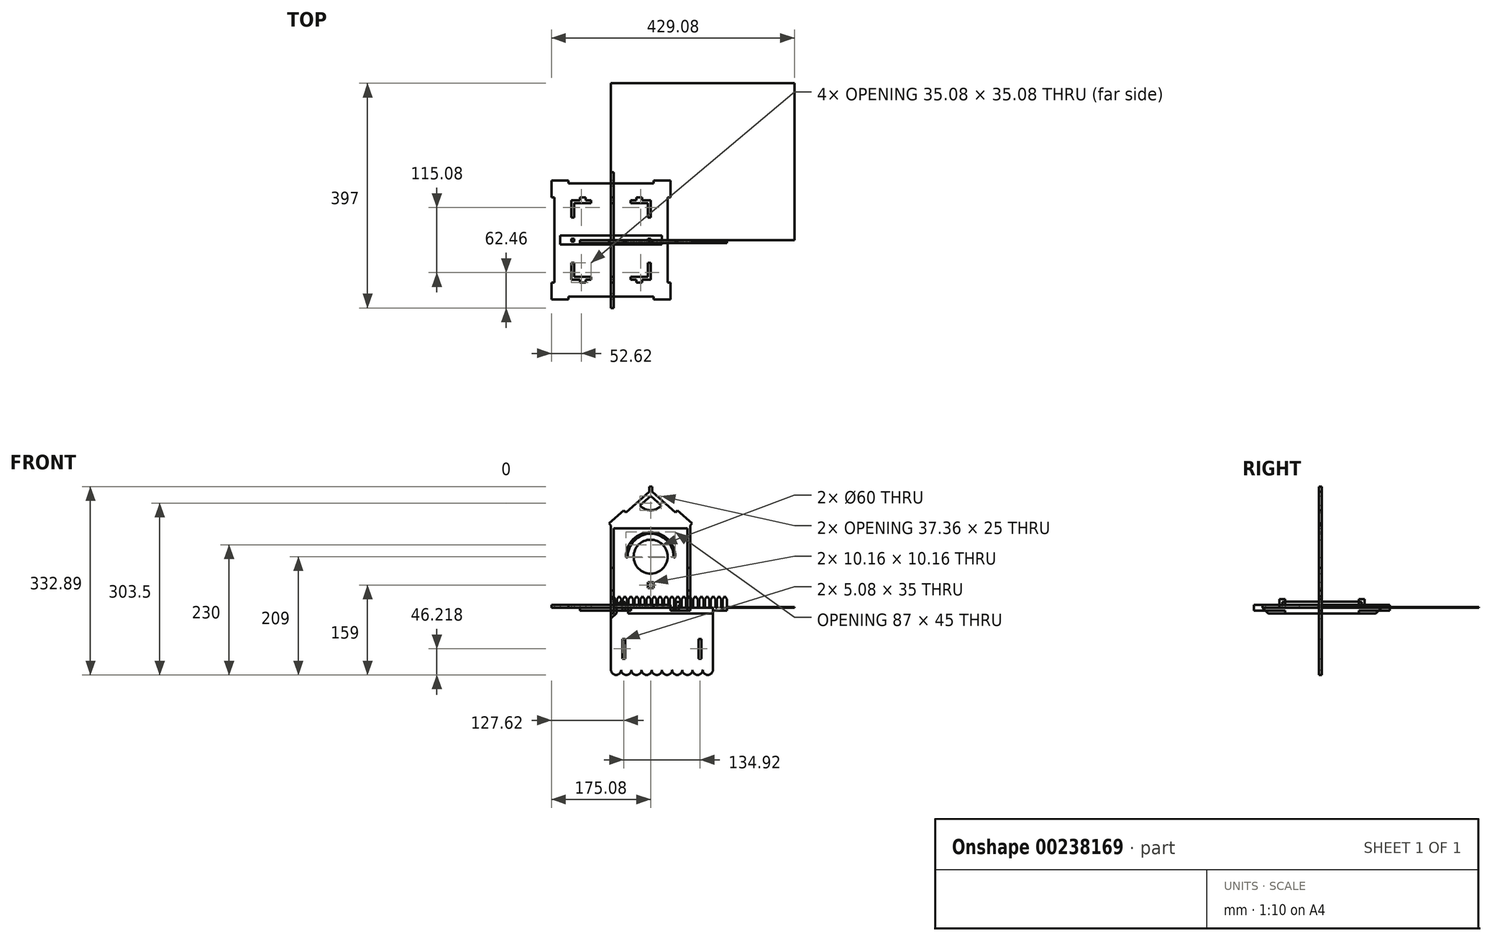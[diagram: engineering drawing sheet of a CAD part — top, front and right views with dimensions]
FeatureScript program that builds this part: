
annotation { "Feature Type Name" : "Feature", "Feature Type Description" : "" }
export const myFeature = defineFeature(function(context is Context, id is Id, definition is map)
    precondition{}
    {
        {
            var Q0;
            Q0=qCreatedBy(makeId("Front.planeOp"),FACE);
            var sketch = newSketch(context, id + "F0", { "sketchPlane" : qUnion([Q0])});
            skLineSegment(sketch, "E0.left", {"start": v(0, 30) * mm, "end": v(0, 70) * mm});
            skLineSegment(sketch, "E1", {"start": v(0, 30) * mm, "end": v(5.08, 30) * mm});
            skLineSegment(sketch, "E2", {"start": v(0, 70) * mm, "end": v(5.08, 70) * mm});
            skLineSegment(sketch, "E3", {"start": v(5.08, 70) * mm, "end": v(5.08, 140) * mm});
            skLineSegment(sketch, "E4", {"start": v(5.08, 30) * mm, "end": v(5.08, -5.08) * mm});
            skLineSegment(sketch, "E5", {"start": v(134.92, 140) * mm, "end": v(134.92, 70) * mm});
            skLineSegment(sketch, "E6", {"start": v(134.92, 70) * mm, "end": v(140, 70) * mm});
            skLineSegment(sketch, "E7", {"start": v(140, 70) * mm, "end": v(140, 30) * mm});
            skLineSegment(sketch, "E8", {"start": v(140, 30) * mm, "end": v(134.92, 30) * mm});
            skLineSegment(sketch, "E9", {"start": v(134.92, 30) * mm, "end": v(134.92, -5.08) * mm});
            skLineSegment(sketch, "E10", {"start": v(70, 145.26) * mm, "end": v(70, -12.71) * mm, "construction": true});
            skCircle(sketch, "E11", {"center": v(70, 90) * mm, "radius": 30 * mm});
            skLineSegment(sketch, "E12.bottom", {"start": v(75.08, 45.08) * mm, "end": v(64.92, 45.08) * mm});
            skLineSegment(sketch, "E12.top", {"start": v(75.08, 34.92) * mm, "end": v(64.92, 34.92) * mm});
            skLineSegment(sketch, "E12.left", {"start": v(75.08, 45.08) * mm, "end": v(75.08, 34.92) * mm});
            skLineSegment(sketch, "E12.right", {"start": v(64.92, 45.08) * mm, "end": v(64.92, 34.92) * mm});
            skPoint(sketch, "E12.middle", {"position": v(70, 40) * mm});
            skLineSegment(sketch, "E13", {"start": v(5.08, -5.08) * mm, "end": v(20.32, -5.08) * mm});
            skLineSegment(sketch, "E14", {"start": v(20.32, -5.08) * mm, "end": v(20.32, 5.08) * mm});
            skLineSegment(sketch, "E15", {"start": v(20.32, 5.08) * mm, "end": v(15.24, 5.08) * mm});
            skLineSegment(sketch, "E16", {"start": v(15.24, 5.08) * mm, "end": v(15.24, 10.16) * mm});
            skLineSegment(sketch, "E17", {"start": v(15.24, 10.16) * mm, "end": v(25.4, 10.16) * mm});
            skLineSegment(sketch, "E18", {"start": v(25.4, 10.16) * mm, "end": v(25.4, -5.08) * mm});
            skLineSegment(sketch, "E19", {"start": v(25.4, -5.08) * mm, "end": v(35.08, -5.08) * mm});
            skLineSegment(sketch, "E20", {"start": v(35.08, -5.08) * mm, "end": v(35.08, 0) * mm});
            skLineSegment(sketch, "E21", {"start": v(134.92, -5.08) * mm, "end": v(119.68, -5.08) * mm});
            skLineSegment(sketch, "E22", {"start": v(119.68, -5.08) * mm, "end": v(119.68, 5.08) * mm});
            skLineSegment(sketch, "E23", {"start": v(119.68, 5.08) * mm, "end": v(124.76, 5.08) * mm});
            skLineSegment(sketch, "E24", {"start": v(124.76, 5.08) * mm, "end": v(124.76, 10.16) * mm});
            skLineSegment(sketch, "E25", {"start": v(124.76, 10.16) * mm, "end": v(114.6, 10.16) * mm});
            skLineSegment(sketch, "E26", {"start": v(114.6, 10.16) * mm, "end": v(114.6, -5.08) * mm});
            skLineSegment(sketch, "E27", {"start": v(114.6, -5.08) * mm, "end": v(104.92, -5.08) * mm});
            skLineSegment(sketch, "E28", {"start": v(104.92, -5.08) * mm, "end": v(104.92, 0) * mm});
            skLineSegment(sketch, "E29", {"start": v(5.08, 140) * mm, "end": v(134.92, 140) * mm});
            skLineSegment(sketch, "E30", {"start": v(35.08, 0) * mm, "end": v(104.92, 0) * mm});
            skSolve(sketch);
        }
        {
            var Q0;
            Q0 = qSketchRegion(id + "F0", true);
            extrude(context, id + "F1", {"entities" : qUnion([Q0]), "depth" : 5.08 * mm});
        }
        {
            var Q0;
            Q0=qCreatedBy(makeId("Front.planeOp"),FACE);
            var sketch = newSketch(context, id + "F2", { "sketchPlane" : qUnion([Q0])});
            skLineSegment(sketch, "E31.left", {"start": v(0, 0) * mm, "end": v(0, 30) * mm});
            skLineSegment(sketch, "E32", {"start": v(0, 70) * mm, "end": v(5.08, 70) * mm});
            skLineSegment(sketch, "E33", {"start": v(5.08, 70) * mm, "end": v(5.08, 30) * mm});
            skLineSegment(sketch, "E34", {"start": v(5.08, 30) * mm, "end": v(0, 30) * mm});
            skLineSegment(sketch, "E35.trimOffspring", {"start": v(0, 70) * mm, "end": v(0, 145) * mm});
            skLineSegment(sketch, "E36", {"start": v(70, -4.41) * mm, "end": v(70, 218.12) * mm, "construction": true});
            skLineSegment(sketch, "E37", {"start": v(140, 0) * mm, "end": v(140, 30) * mm});
            skLineSegment(sketch, "E38", {"start": v(140, 30) * mm, "end": v(134.92, 30) * mm});
            skLineSegment(sketch, "E39", {"start": v(134.92, 30) * mm, "end": v(134.92, 70) * mm});
            skLineSegment(sketch, "E40", {"start": v(134.92, 70) * mm, "end": v(140, 70) * mm});
            skLineSegment(sketch, "E41", {"start": v(140, 70) * mm, "end": v(140, 145) * mm});
            skLineSegment(sketch, "E42", {"start": v(26.15, 168.26) * mm, "end": v(67.46, 205) * mm});
            skLineSegment(sketch, "E43", {"start": v(0, 145) * mm, "end": v(-3.38, 148.8) * mm});
            skLineSegment(sketch, "E44", {"start": v(-3.38, 148.8) * mm, "end": v(22.78, 172.06) * mm});
            skLineSegment(sketch, "E45", {"start": v(22.78, 172.06) * mm, "end": v(26.15, 168.26) * mm});
            skLineSegment(sketch, "E46", {"start": v(0, 145) * mm, "end": v(26.15, 168.26) * mm, "construction": true});
            skLineSegment(sketch, "E47", {"start": v(140, 145) * mm, "end": v(143.38, 148.8) * mm});
            skLineSegment(sketch, "E48", {"start": v(143.38, 148.8) * mm, "end": v(117.22, 172.06) * mm});
            skLineSegment(sketch, "E49", {"start": v(117.22, 172.06) * mm, "end": v(113.85, 168.26) * mm});
            skLineSegment(sketch, "E50", {"start": v(67.46, 205) * mm, "end": v(67.46, 213.89) * mm});
            skLineSegment(sketch, "E51", {"start": v(67.46, 213.89) * mm, "end": v(70, 213.89) * mm});
            skLineSegment(sketch, "E52", {"start": v(113.85, 168.26) * mm, "end": v(72.54, 205) * mm});
            skLineSegment(sketch, "E53", {"start": v(72.54, 205) * mm, "end": v(72.54, 213.89) * mm});
            skLineSegment(sketch, "E54", {"start": v(72.54, 213.89) * mm, "end": v(70, 213.89) * mm});
            skLineSegment(sketch, "E55", {"start": v(70, 197) * mm, "end": v(51.32, 180.39) * mm});
            skLineSegment(sketch, "E56", {"start": v(70, 197) * mm, "end": v(88.68, 180.39) * mm});
            skArc(sketch, "E57", {"start": v(88.68, 180.39) * mm, "mid": v(70, 172) * mm, "end": v(51.32, 180.39) * mm});
            skLineSegment(sketch, "E58", {"start": v(0, 0) * mm, "end": v(0, -5.08) * mm});
            skLineSegment(sketch, "E59", {"start": v(0, -5.08) * mm, "end": v(30, -5.08) * mm});
            skLineSegment(sketch, "E60", {"start": v(30, -5.08) * mm, "end": v(30, 0) * mm});
            skLineSegment(sketch, "E61", {"start": v(140, 0) * mm, "end": v(140, -5.08) * mm});
            skLineSegment(sketch, "E62", {"start": v(140, -5.08) * mm, "end": v(110, -5.08) * mm});
            skLineSegment(sketch, "E63", {"start": v(110, -5.08) * mm, "end": v(110, 0) * mm});
            skLineSegment(sketch, "E64", {"start": v(30, 0) * mm, "end": v(110, 0) * mm});
            skSolve(sketch);
        }
        {
            var Q0;
            Q0 = qSketchRegion(id + "F2", true);
            extrude(context, id + "F3", {"entities" : qUnion([Q0]), "depth" : 5.08 * mm});
        }
        {
            var Q0;
            Q0=qCreatedBy(makeId("Front.planeOp"),FACE);
            var sketch = newSketch(context, id + "F4", { "sketchPlane" : qUnion([Q0])});
            skLineSegment(sketch, "E65.left", {"start": v(0, 0) * mm, "end": v(0, 30) * mm});
            skLineSegment(sketch, "E66", {"start": v(0, 70) * mm, "end": v(5.08, 70) * mm});
            skLineSegment(sketch, "E67", {"start": v(5.08, 70) * mm, "end": v(5.08, 30) * mm});
            skLineSegment(sketch, "E68", {"start": v(5.08, 30) * mm, "end": v(0, 30) * mm});
            skLineSegment(sketch, "E69.trimOffspring", {"start": v(0, 70) * mm, "end": v(0, 145) * mm});
            skLineSegment(sketch, "E70", {"start": v(70, -55.12) * mm, "end": v(70, 167.4) * mm, "construction": true});
            skLineSegment(sketch, "E71", {"start": v(140, 0) * mm, "end": v(140, 30) * mm});
            skLineSegment(sketch, "E72", {"start": v(140, 30) * mm, "end": v(134.92, 30) * mm});
            skLineSegment(sketch, "E73", {"start": v(134.92, 30) * mm, "end": v(134.92, 70) * mm});
            skLineSegment(sketch, "E74", {"start": v(134.92, 70) * mm, "end": v(140, 70) * mm});
            skLineSegment(sketch, "E75", {"start": v(140, 70) * mm, "end": v(140, 145) * mm});
            skLineSegment(sketch, "E76", {"start": v(26.15, 168.26) * mm, "end": v(67.46, 205) * mm});
            skLineSegment(sketch, "E77", {"start": v(0, 145) * mm, "end": v(-3.38, 148.8) * mm});
            skLineSegment(sketch, "E78", {"start": v(-3.38, 148.8) * mm, "end": v(22.78, 172.06) * mm});
            skLineSegment(sketch, "E79", {"start": v(22.78, 172.06) * mm, "end": v(26.15, 168.26) * mm});
            skLineSegment(sketch, "E80", {"start": v(0, 145) * mm, "end": v(26.15, 168.26) * mm, "construction": true});
            skLineSegment(sketch, "E81", {"start": v(140, 145) * mm, "end": v(143.38, 148.8) * mm});
            skLineSegment(sketch, "E82", {"start": v(143.38, 148.8) * mm, "end": v(117.22, 172.06) * mm});
            skLineSegment(sketch, "E83", {"start": v(117.22, 172.06) * mm, "end": v(113.85, 168.26) * mm});
            skLineSegment(sketch, "E84", {"start": v(67.46, 205) * mm, "end": v(67.46, 213.9) * mm});
            skLineSegment(sketch, "E85", {"start": v(67.46, 213.89) * mm, "end": v(70, 213.89) * mm});
            skLineSegment(sketch, "E86", {"start": v(113.85, 168.26) * mm, "end": v(72.54, 205) * mm});
            skLineSegment(sketch, "E87", {"start": v(72.54, 205) * mm, "end": v(72.54, 213.9) * mm});
            skLineSegment(sketch, "E88", {"start": v(72.54, 213.9) * mm, "end": v(70, 213.9) * mm});
            skLineSegment(sketch, "E89", {"start": v(70, 197) * mm, "end": v(51.32, 180.39) * mm});
            skLineSegment(sketch, "E90", {"start": v(70, 197) * mm, "end": v(88.68, 180.39) * mm});
            skArc(sketch, "E91", {"start": v(88.68, 180.39) * mm, "mid": v(70, 172) * mm, "end": v(51.32, 180.39) * mm});
            skCircle(sketch, "E92", {"center": v(70, 90) * mm, "radius": 30 * mm});
            skArc(sketch, "E93", {"start": v(28, 90) * mm, "mid": v(70, 132) * mm, "end": v(112, 90) * mm});
            skArc(sketch, "E94.0.startCap", {"start": v(29.5, 90) * mm, "mid": v(28, 88.5) * mm, "end": v(26.5, 90) * mm});
            skArc(sketch, "E94.0.endCap", {"start": v(113.5, 90) * mm, "mid": v(112, 88.5) * mm, "end": v(110.5, 90) * mm});
            skArc(sketch, "E94.0.left", {"start": v(26.5, 90) * mm, "mid": v(70, 133.5) * mm, "end": v(113.5, 90) * mm});
            skArc(sketch, "E94.0.right", {"start": v(29.5, 90) * mm, "mid": v(70, 130.5) * mm, "end": v(110.5, 90) * mm});
            skLineSegment(sketch, "E95.bottom", {"start": v(75.08, 45.08) * mm, "end": v(64.92, 45.08) * mm});
            skLineSegment(sketch, "E95.top", {"start": v(75.08, 34.92) * mm, "end": v(64.92, 34.92) * mm});
            skLineSegment(sketch, "E95.left", {"start": v(75.08, 45.08) * mm, "end": v(75.08, 34.92) * mm});
            skLineSegment(sketch, "E95.right", {"start": v(64.92, 45.08) * mm, "end": v(64.92, 34.92) * mm});
            skPoint(sketch, "E95.middle", {"position": v(70, 40) * mm});
            skLineSegment(sketch, "E96", {"start": v(0, 0) * mm, "end": v(0, -5.08) * mm});
            skLineSegment(sketch, "E97", {"start": v(0, -5.08) * mm, "end": v(30, -5.08) * mm});
            skLineSegment(sketch, "E98", {"start": v(30, -5.08) * mm, "end": v(30, 0) * mm});
            skLineSegment(sketch, "E99", {"start": v(140, 0) * mm, "end": v(140, -5.08) * mm});
            skLineSegment(sketch, "E100", {"start": v(140, -5.08) * mm, "end": v(110, -5.08) * mm});
            skLineSegment(sketch, "E101", {"start": v(110, -5.08) * mm, "end": v(110, 0) * mm});
            skLineSegment(sketch, "E102", {"start": v(30, 0) * mm, "end": v(110, 0) * mm});
            skSolve(sketch);
        }
        {
            var Q0;
            Q0 = qSketchRegion(id + "F4", true);
            extrude(context, id + "F5", {"entities" : qUnion([Q0]), "depth" : 5.08 * mm});
        }
        {
            var Q0;
            Q0=qCreatedBy(makeId("Right.planeOp"),FACE);
            var sketch = newSketch(context, id + "F6", { "sketchPlane" : qUnion([Q0])});
            skLineSegment(sketch, "E103.bottom", {"start": v(64.92, 10.26) * mm, "end": v(-64.92, 10.26) * mm});
            skLineSegment(sketch, "E103.top", {"start": v(64.92, -10.26) * mm, "end": v(-64.92, -10.26) * mm});
            skLineSegment(sketch, "E103.left", {"start": v(64.92, 10.26) * mm, "end": v(64.92, 5.08) * mm});
            skLineSegment(sketch, "E103.right", {"start": v(-64.92, 10.26) * mm, "end": v(-64.92, 5.08) * mm});
            skPoint(sketch, "E103.middle", {"position": v(0, 0) * mm});
            skLineSegment(sketch, "E104.bottom", {"start": v(120, 5.08) * mm, "end": v(64.92, 5.08) * mm});
            skLineSegment(sketch, "E104.top", {"start": v(120, -5.08) * mm, "end": v(64.92, -5.08) * mm});
            skLineSegment(sketch, "E104.left", {"start": v(120, 5.08) * mm, "end": v(120, -5.08) * mm});
            skLineSegment(sketch, "E104.right", {"start": v(-120, 5.08) * mm, "end": v(-120, -5.08) * mm});
            skLineSegment(sketch, "E105.trimOffspring", {"start": v(-64.92, 5.08) * mm, "end": v(-120, 5.08) * mm});
            skLineSegment(sketch, "E106.trimOffspring", {"start": v(-64.92, -5.08) * mm, "end": v(-120, -5.08) * mm});
            skLineSegment(sketch, "E107.trimOffspring", {"start": v(-64.92, -5.08) * mm, "end": v(-64.92, -10.26) * mm});
            skLineSegment(sketch, "E108.trimOffspring", {"start": v(64.92, -5.08) * mm, "end": v(64.92, -10.26) * mm});
            skSolve(sketch);
        }
        {
            var Q0;
            Q0 = qSketchRegion(id + "F6", true);
            extrude(context, id + "F7", {"entities" : qUnion([Q0]), "depth" : 5.08 * mm});
        }
        {
            var Q0;
            Q0=qCreatedBy(makeId("Front.planeOp"),FACE);
            var sketch = newSketch(context, id + "F8", { "sketchPlane" : qUnion([Q0])});
            skLineSegment(sketch, "E109", {"start": v(-91.76, 0) * mm, "end": v(91.72, 0) * mm, "construction": true});
            skLineSegment(sketch, "E110", {"start": v(-55.08, 5.08) * mm, "end": v(0, 5.08) * mm});
            skLineSegment(sketch, "E111", {"start": v(0, 5.08) * mm, "end": v(0, 19.08) * mm});
            skLineSegment(sketch, "E112", {"start": v(0, 19.08) * mm, "end": v(10.16, 9.54) * mm});
            skLineSegment(sketch, "E113.MirrorCS", {"start": v(0, -19.08) * mm, "end": v(10.16, -9.54) * mm});
            skLineSegment(sketch, "E114.MirrorCS", {"start": v(-55.08, -5.08) * mm, "end": v(0, -5.08) * mm});
            skLineSegment(sketch, "E115.MirrorCS", {"start": v(0, -5.08) * mm, "end": v(0, -19.08) * mm});
            skLineSegment(sketch, "E116", {"start": v(-55.08, 5.08) * mm, "end": v(-55.08, -5.08) * mm});
            skLineSegment(sketch, "E117", {"start": v(10.16, 9.54) * mm, "end": v(10.16, -9.54) * mm});
            skSolve(sketch);
        }
        {
            var Q0;
            Q0 = qSketchRegion(id + "F8", true);
            extrude(context, id + "F9", {"entities" : qUnion([Q0]), "depth" : 5.08 * mm});
        }
        {
            var Q0;
            Q0=qCreatedBy(makeId("Top.planeOp"),FACE);
            var sketch = newSketch(context, id + "F10", { "sketchPlane" : qUnion([Q0])});
            skLineSegment(sketch, "E118.bottom", {"start": v(100, 100) * mm, "end": v(-100, 100) * mm, "construction": true});
            skLineSegment(sketch, "E118.top", {"start": v(100, -100) * mm, "end": v(-100, -100) * mm, "construction": true});
            skLineSegment(sketch, "E118.left", {"start": v(100, 100) * mm, "end": v(100, -100) * mm, "construction": true});
            skLineSegment(sketch, "E118.right", {"start": v(-100, 100) * mm, "end": v(-100, -100) * mm, "construction": true});
            skPoint(sketch, "E118.middle", {"position": v(0, 0) * mm});
            skLineSegment(sketch, "E119.bottom", {"start": v(70, -70) * mm, "end": v(-70, -70) * mm, "construction": true});
            skLineSegment(sketch, "E119.top", {"start": v(70, 70) * mm, "end": v(-70, 70) * mm, "construction": true});
            skLineSegment(sketch, "E119.left", {"start": v(70, -70) * mm, "end": v(70, 70) * mm, "construction": true});
            skLineSegment(sketch, "E119.right", {"start": v(-70, -70) * mm, "end": v(-70, 70) * mm, "construction": true});
            skLineSegment(sketch, "E120", {"start": v(-70, 70) * mm, "end": v(-54.76, 70) * mm});
            skLineSegment(sketch, "E121", {"start": v(-34.92, 64.92) * mm, "end": v(-64.92, 64.92) * mm});
            skLineSegment(sketch, "E122", {"start": v(-64.92, 64.92) * mm, "end": v(-64.92, 40) * mm});
            skLineSegment(sketch, "E123", {"start": v(-64.92, 40) * mm, "end": v(-70, 40) * mm});
            skLineSegment(sketch, "E124", {"start": v(-70, 40) * mm, "end": v(-70, 70) * mm});
            skLineSegment(sketch, "E125", {"start": v(0, 100.63) * mm, "end": v(0, -98.34) * mm, "construction": true});
            skLineSegment(sketch, "E126", {"start": v(-101.52, 0) * mm, "end": v(102.53, 0) * mm, "construction": true});
            skPoint(sketch, "E126.endSnap0", {"position": v(70, 0) * mm});
            skPoint(sketch, "E127.MirrorP", {"position": v(-70, 0) * mm});
            skLineSegment(sketch, "E128", {"start": v(-100, 75.08) * mm, "end": v(-105.08, 75.08) * mm});
            skLineSegment(sketch, "E129", {"start": v(-105.08, 75.08) * mm, "end": v(-105.08, 105.08) * mm});
            skLineSegment(sketch, "E130", {"start": v(-105.08, 105.08) * mm, "end": v(-75.08, 105.08) * mm});
            skLineSegment(sketch, "E131", {"start": v(-75.08, 105.08) * mm, "end": v(-75.08, 100) * mm});
            skLineSegment(sketch, "E132.MirrorCS", {"start": v(75.08, 105.08) * mm, "end": v(75.08, 100) * mm});
            skLineSegment(sketch, "E133.MirrorCS", {"start": v(105.08, 105.08) * mm, "end": v(75.08, 105.08) * mm});
            skLineSegment(sketch, "E134.MirrorCS", {"start": v(100, 75.08) * mm, "end": v(105.08, 75.08) * mm});
            skLineSegment(sketch, "E135.MirrorCS", {"start": v(105.08, 75.08) * mm, "end": v(105.08, 105.08) * mm});
            skLineSegment(sketch, "E136", {"start": v(-75.08, 100) * mm, "end": v(75.08, 100) * mm});
            skLineSegment(sketch, "E137.MirrorCS", {"start": v(100, -75.08) * mm, "end": v(105.08, -75.08) * mm});
            skLineSegment(sketch, "E138.MirrorCS", {"start": v(105.08, -75.08) * mm, "end": v(105.08, -105.08) * mm});
            skLineSegment(sketch, "E139.MirrorCS", {"start": v(105.08, -105.08) * mm, "end": v(75.08, -105.08) * mm});
            skLineSegment(sketch, "E140.MirrorCS", {"start": v(75.08, -105.08) * mm, "end": v(75.08, -100) * mm});
            skLineSegment(sketch, "E141.MirrorCS", {"start": v(-75.08, -100) * mm, "end": v(75.08, -100) * mm});
            skLineSegment(sketch, "E142.MirrorCS", {"start": v(-75.08, -105.08) * mm, "end": v(-75.08, -100) * mm});
            skLineSegment(sketch, "E143.MirrorCS", {"start": v(-105.08, -105.08) * mm, "end": v(-75.08, -105.08) * mm});
            skLineSegment(sketch, "E144.MirrorCS", {"start": v(-100, -75.08) * mm, "end": v(-105.08, -75.08) * mm});
            skLineSegment(sketch, "E145.MirrorCS", {"start": v(-105.08, -75.08) * mm, "end": v(-105.08, -105.08) * mm});
            skLineSegment(sketch, "E146", {"start": v(-100, 75.08) * mm, "end": v(-100, -75.08) * mm});
            skLineSegment(sketch, "E147", {"start": v(100, 75.08) * mm, "end": v(100, -75.08) * mm});
            skLineSegment(sketch, "E148", {"start": v(-54.76, 70) * mm, "end": v(-54.76, 75.08) * mm});
            skLineSegment(sketch, "E149", {"start": v(-54.76, 75.08) * mm, "end": v(-44.6, 75.08) * mm});
            skLineSegment(sketch, "E150", {"start": v(-44.6, 75.08) * mm, "end": v(-44.6, 70) * mm});
            skLineSegment(sketch, "E151", {"start": v(-44.6, 70) * mm, "end": v(-34.92, 70) * mm});
            skLineSegment(sketch, "E152", {"start": v(-34.92, 70) * mm, "end": v(-34.92, 64.92) * mm});
            skLineSegment(sketch, "E153.MirrorCS", {"start": v(54.76, 75.08) * mm, "end": v(44.6, 75.08) * mm});
            skLineSegment(sketch, "E154.MirrorCS", {"start": v(54.76, 70) * mm, "end": v(54.76, 75.08) * mm});
            skLineSegment(sketch, "E155.MirrorCS", {"start": v(70, 40) * mm, "end": v(70, 70) * mm});
            skLineSegment(sketch, "E156.MirrorCS", {"start": v(34.92, 64.92) * mm, "end": v(64.92, 64.92) * mm});
            skLineSegment(sketch, "E157.MirrorCS", {"start": v(70, 70) * mm, "end": v(54.76, 70) * mm});
            skLineSegment(sketch, "E158.MirrorCS", {"start": v(44.6, 75.08) * mm, "end": v(44.6, 70) * mm});
            skLineSegment(sketch, "E159.MirrorCS", {"start": v(64.92, 40) * mm, "end": v(70, 40) * mm});
            skLineSegment(sketch, "E160.MirrorCS", {"start": v(44.6, 70) * mm, "end": v(34.92, 70) * mm});
            skLineSegment(sketch, "E161.MirrorCS", {"start": v(64.92, 64.92) * mm, "end": v(64.92, 40) * mm});
            skLineSegment(sketch, "E162.MirrorCS", {"start": v(34.92, 70) * mm, "end": v(34.92, 64.92) * mm});
            skLineSegment(sketch, "E163.MirrorCS", {"start": v(-44.6, -70) * mm, "end": v(-34.92, -70) * mm});
            skLineSegment(sketch, "E164.MirrorCS", {"start": v(-70, -70) * mm, "end": v(-54.76, -70) * mm});
            skLineSegment(sketch, "E165.MirrorCS", {"start": v(70, -70) * mm, "end": v(54.76, -70) * mm});
            skLineSegment(sketch, "E166.MirrorCS", {"start": v(44.6, -70) * mm, "end": v(34.92, -70) * mm});
            skLineSegment(sketch, "E167.MirrorCS", {"start": v(34.92, -64.92) * mm, "end": v(64.92, -64.92) * mm});
            skLineSegment(sketch, "E168.MirrorCS", {"start": v(-54.76, -70) * mm, "end": v(-54.76, -75.08) * mm});
            skLineSegment(sketch, "E169.MirrorCS", {"start": v(64.92, -40) * mm, "end": v(70, -40) * mm});
            skLineSegment(sketch, "E170.MirrorCS", {"start": v(-64.92, -40) * mm, "end": v(-70, -40) * mm});
            skLineSegment(sketch, "E171.MirrorCS", {"start": v(-54.76, -75.08) * mm, "end": v(-44.6, -75.08) * mm});
            skLineSegment(sketch, "E172.MirrorCS", {"start": v(-44.6, -75.08) * mm, "end": v(-44.6, -70) * mm});
            skLineSegment(sketch, "E173.MirrorCS", {"start": v(70, -40) * mm, "end": v(70, -70) * mm});
            skLineSegment(sketch, "E174.MirrorCS", {"start": v(-34.92, -64.92) * mm, "end": v(-64.92, -64.92) * mm});
            skLineSegment(sketch, "E175.MirrorCS", {"start": v(54.76, -70) * mm, "end": v(54.76, -75.08) * mm});
            skLineSegment(sketch, "E176.MirrorCS", {"start": v(54.76, -75.08) * mm, "end": v(44.6, -75.08) * mm});
            skLineSegment(sketch, "E177.MirrorCS", {"start": v(-34.92, -70) * mm, "end": v(-34.92, -64.92) * mm});
            skLineSegment(sketch, "E178.MirrorCS", {"start": v(-64.92, -64.92) * mm, "end": v(-64.92, -40) * mm});
            skLineSegment(sketch, "E179.MirrorCS", {"start": v(44.6, -75.08) * mm, "end": v(44.6, -70) * mm});
            skLineSegment(sketch, "E180.MirrorCS", {"start": v(64.92, -64.92) * mm, "end": v(64.92, -40) * mm});
            skLineSegment(sketch, "E181.MirrorCS", {"start": v(34.92, -70) * mm, "end": v(34.92, -64.92) * mm});
            skLineSegment(sketch, "E182.MirrorCS", {"start": v(-70, -40) * mm, "end": v(-70, -70) * mm});
            skSolve(sketch);
        }
        {
            var Q0;
            Q0 = qSketchRegion(id + "F10", true);
            extrude(context, id + "F11", {"entities" : qUnion([Q0]), "depth" : 5.08 * mm});
        }
        {
            var Q0;
            Q0=qCreatedBy(makeId("Right.planeOp"),FACE);
            var sketch = newSketch(context, id + "F12", { "sketchPlane" : qUnion([Q0])});
            skLineSegment(sketch, "E183", {"start": v(0, 25.44) * mm, "end": v(0, -25.01) * mm, "construction": true});
            skLineSegment(sketch, "E184", {"start": v(0, 0) * mm, "end": v(70, 0) * mm});
            skLineSegment(sketch, "E185", {"start": v(70, 0) * mm, "end": v(70, 10.16) * mm});
            skLineSegment(sketch, "E186", {"start": v(70, 10.16) * mm, "end": v(64.92, 10.16) * mm});
            skLineSegment(sketch, "E187", {"start": v(64.92, 10.16) * mm, "end": v(64.92, 15.24) * mm});
            skLineSegment(sketch, "E188", {"start": v(64.92, 15.24) * mm, "end": v(75.08, 15.24) * mm});
            skLineSegment(sketch, "E189", {"start": v(75.08, 15.24) * mm, "end": v(75.08, 0) * mm});
            skLineSegment(sketch, "E190", {"start": v(75.08, 0) * mm, "end": v(105.08, 0) * mm});
            skLineSegment(sketch, "E191", {"start": v(105.08, 0) * mm, "end": v(94.92, -10.16) * mm});
            skLineSegment(sketch, "E192", {"start": v(94.92, -10.16) * mm, "end": v(0, -10.16) * mm});
            skLineSegment(sketch, "E193.MirrorCS", {"start": v(0, 0) * mm, "end": v(-70, 0) * mm});
            skLineSegment(sketch, "E194.MirrorCS", {"start": v(-70, 10.16) * mm, "end": v(-64.92, 10.16) * mm});
            skLineSegment(sketch, "E195.MirrorCS", {"start": v(-105.08, 0) * mm, "end": v(-94.92, -10.16) * mm});
            skLineSegment(sketch, "E196.MirrorCS", {"start": v(-94.92, -10.16) * mm, "end": v(0, -10.16) * mm});
            skLineSegment(sketch, "E197.MirrorCS", {"start": v(-64.92, 10.16) * mm, "end": v(-64.92, 15.24) * mm});
            skLineSegment(sketch, "E198.MirrorCS", {"start": v(-75.08, 15.24) * mm, "end": v(-75.08, 0) * mm});
            skLineSegment(sketch, "E199.MirrorCS", {"start": v(-70, 0) * mm, "end": v(-70, 10.16) * mm});
            skLineSegment(sketch, "E200.MirrorCS", {"start": v(-75.08, 0) * mm, "end": v(-105.08, 0) * mm});
            skLineSegment(sketch, "E201.MirrorCS", {"start": v(-64.92, 15.24) * mm, "end": v(-75.08, 15.24) * mm});
            skSolve(sketch);
        }
        {
            var Q0;
            Q0 = qSketchRegion(id + "F12", true);
            extrude(context, id + "F13", {"entities" : qUnion([Q0]), "depth" : 5.08 * mm});
        }
        {
            var Q0;
            Q0=qCreatedBy(makeId("Front.planeOp"),FACE);
            var sketch = newSketch(context, id + "F14", { "sketchPlane" : qUnion([Q0])});
            skLineSegment(sketch, "E202", {"start": v(0, 0) * mm, "end": v(0, 15.24) * mm});
            skLineSegment(sketch, "E203", {"start": v(0, 15.24) * mm, "end": v(3.9, 20.32) * mm});
            skLineSegment(sketch, "E204", {"start": v(3.9, 20.32) * mm, "end": v(7.79, 15.24) * mm});
            skLineSegment(sketch, "E205", {"start": v(7.79, 15.24) * mm, "end": v(7.79, 0) * mm});
            skLineSegment(sketch, "E206", {"start": v(7.79, 0) * mm, "end": v(10.38, 0) * mm});
            skLineSegment(sketch, "E207", {"start": v(0, 15.24) * mm, "end": v(7.79, 15.24) * mm, "construction": true});
            skPoint(sketch, "E208", {"position": v(3.9, 15.24) * mm});
            skLineSegment(sketch, "E209.1.0.0", {"start": v(10.38, 15.24) * mm, "end": v(18.17, 15.24) * mm, "construction": true});
            skLineSegment(sketch, "E209.1.0.1", {"start": v(18.17, 15.24) * mm, "end": v(18.17, 0) * mm});
            skLineSegment(sketch, "E209.1.0.2", {"start": v(14.28, 20.32) * mm, "end": v(18.17, 15.24) * mm});
            skLineSegment(sketch, "E209.1.0.3", {"start": v(10.38, 15.24) * mm, "end": v(14.28, 20.32) * mm});
            skLineSegment(sketch, "E209.1.0.4", {"start": v(10.38, 0) * mm, "end": v(10.38, 15.24) * mm});
            skPoint(sketch, "E209.1.0.5", {"position": v(14.28, 15.24) * mm});
            skLineSegment(sketch, "E209.1.0.6", {"start": v(18.17, 0) * mm, "end": v(20.77, 0) * mm});
            skLineSegment(sketch, "E209.2.0.0", {"start": v(20.77, 15.24) * mm, "end": v(28.56, 15.24) * mm, "construction": true});
            skLineSegment(sketch, "E209.2.0.1", {"start": v(28.56, 15.24) * mm, "end": v(28.56, 0) * mm});
            skLineSegment(sketch, "E209.2.0.2", {"start": v(24.66, 20.32) * mm, "end": v(28.56, 15.24) * mm});
            skLineSegment(sketch, "E209.2.0.3", {"start": v(20.77, 15.24) * mm, "end": v(24.66, 20.32) * mm});
            skLineSegment(sketch, "E209.2.0.4", {"start": v(20.77, 0) * mm, "end": v(20.77, 15.24) * mm});
            skPoint(sketch, "E209.2.0.5", {"position": v(24.66, 15.24) * mm});
            skLineSegment(sketch, "E209.2.0.6", {"start": v(28.56, 0) * mm, "end": v(31.15, 0) * mm});
            skLineSegment(sketch, "E209.3.0.0", {"start": v(31.15, 15.24) * mm, "end": v(38.94, 15.24) * mm, "construction": true});
            skLineSegment(sketch, "E209.3.0.1", {"start": v(38.94, 15.24) * mm, "end": v(38.94, 0) * mm});
            skLineSegment(sketch, "E209.3.0.2", {"start": v(35.05, 20.32) * mm, "end": v(38.94, 15.24) * mm});
            skLineSegment(sketch, "E209.3.0.3", {"start": v(31.15, 15.24) * mm, "end": v(35.05, 20.32) * mm});
            skLineSegment(sketch, "E209.3.0.4", {"start": v(31.15, 0) * mm, "end": v(31.15, 15.24) * mm});
            skPoint(sketch, "E209.3.0.5", {"position": v(35.05, 15.24) * mm});
            skLineSegment(sketch, "E209.3.0.6", {"start": v(38.94, 0) * mm, "end": v(41.54, 0) * mm});
            skLineSegment(sketch, "E209.4.0.0", {"start": v(41.54, 15.24) * mm, "end": v(49.32, 15.24) * mm, "construction": true});
            skLineSegment(sketch, "E209.4.0.1", {"start": v(49.32, 15.24) * mm, "end": v(49.32, 0) * mm});
            skLineSegment(sketch, "E209.4.0.2", {"start": v(45.43, 20.32) * mm, "end": v(49.32, 15.24) * mm});
            skLineSegment(sketch, "E209.4.0.3", {"start": v(41.54, 15.24) * mm, "end": v(45.43, 20.32) * mm});
            skLineSegment(sketch, "E209.4.0.4", {"start": v(41.54, 0) * mm, "end": v(41.54, 15.24) * mm});
            skPoint(sketch, "E209.4.0.5", {"position": v(45.43, 15.24) * mm});
            skLineSegment(sketch, "E209.4.0.6", {"start": v(49.32, 0) * mm, "end": v(51.92, 0) * mm});
            skLineSegment(sketch, "E209.5.0.0", {"start": v(51.92, 15.24) * mm, "end": v(59.7, 15.24) * mm, "construction": true});
            skLineSegment(sketch, "E209.5.0.1", {"start": v(59.7, 15.24) * mm, "end": v(59.7, 0) * mm});
            skLineSegment(sketch, "E209.5.0.2", {"start": v(55.81, 20.32) * mm, "end": v(59.7, 15.24) * mm});
            skLineSegment(sketch, "E209.5.0.3", {"start": v(51.92, 15.24) * mm, "end": v(55.81, 20.32) * mm});
            skLineSegment(sketch, "E209.5.0.4", {"start": v(51.92, 0) * mm, "end": v(51.92, 15.24) * mm});
            skPoint(sketch, "E209.5.0.5", {"position": v(55.81, 15.24) * mm});
            skLineSegment(sketch, "E209.5.0.6", {"start": v(59.7, 0) * mm, "end": v(62.3, 0) * mm});
            skLineSegment(sketch, "E209.6.0.0", {"start": v(62.3, 15.24) * mm, "end": v(70.1, 15.24) * mm, "construction": true});
            skLineSegment(sketch, "E209.6.0.1", {"start": v(70.1, 15.24) * mm, "end": v(70.1, 0) * mm});
            skLineSegment(sketch, "E209.6.0.2", {"start": v(66.2, 20.32) * mm, "end": v(70.1, 15.24) * mm});
            skLineSegment(sketch, "E209.6.0.3", {"start": v(62.3, 15.24) * mm, "end": v(66.2, 20.32) * mm});
            skLineSegment(sketch, "E209.6.0.4", {"start": v(62.3, 0) * mm, "end": v(62.3, 15.24) * mm});
            skPoint(sketch, "E209.6.0.5", {"position": v(66.2, 15.24) * mm});
            skLineSegment(sketch, "E209.6.0.6", {"start": v(70.1, 0) * mm, "end": v(72.69, 0) * mm});
            skLineSegment(sketch, "E209.7.0.0", {"start": v(72.69, 15.24) * mm, "end": v(80.48, 15.24) * mm, "construction": true});
            skLineSegment(sketch, "E209.7.0.1", {"start": v(80.48, 15.24) * mm, "end": v(80.48, 0) * mm});
            skLineSegment(sketch, "E209.7.0.2", {"start": v(76.58, 20.32) * mm, "end": v(80.48, 15.24) * mm});
            skLineSegment(sketch, "E209.7.0.3", {"start": v(72.69, 15.24) * mm, "end": v(76.58, 20.32) * mm});
            skLineSegment(sketch, "E209.7.0.4", {"start": v(72.69, 0) * mm, "end": v(72.69, 15.24) * mm});
            skPoint(sketch, "E209.7.0.5", {"position": v(76.58, 15.24) * mm});
            skLineSegment(sketch, "E209.7.0.6", {"start": v(80.48, 0) * mm, "end": v(83.07, 0) * mm});
            skLineSegment(sketch, "E209.8.0.0", {"start": v(83.07, 15.24) * mm, "end": v(90.86, 15.24) * mm, "construction": true});
            skLineSegment(sketch, "E209.8.0.1", {"start": v(90.86, 15.24) * mm, "end": v(90.86, 0) * mm});
            skLineSegment(sketch, "E209.8.0.2", {"start": v(86.97, 20.32) * mm, "end": v(90.86, 15.24) * mm});
            skLineSegment(sketch, "E209.8.0.3", {"start": v(83.07, 15.24) * mm, "end": v(86.97, 20.32) * mm});
            skLineSegment(sketch, "E209.8.0.4", {"start": v(83.07, 0) * mm, "end": v(83.07, 15.24) * mm});
            skPoint(sketch, "E209.8.0.5", {"position": v(86.97, 15.24) * mm});
            skLineSegment(sketch, "E209.8.0.6", {"start": v(90.86, 0) * mm, "end": v(93.46, 0) * mm});
            skLineSegment(sketch, "E209.9.0.0", {"start": v(93.46, 15.24) * mm, "end": v(101.24, 15.24) * mm, "construction": true});
            skLineSegment(sketch, "E209.9.0.1", {"start": v(101.24, 15.24) * mm, "end": v(101.24, 0) * mm});
            skLineSegment(sketch, "E209.9.0.2", {"start": v(97.35, 20.32) * mm, "end": v(101.24, 15.24) * mm});
            skLineSegment(sketch, "E209.9.0.3", {"start": v(93.46, 15.24) * mm, "end": v(97.35, 20.32) * mm});
            skLineSegment(sketch, "E209.9.0.4", {"start": v(93.46, 0) * mm, "end": v(93.46, 15.24) * mm});
            skPoint(sketch, "E209.9.0.5", {"position": v(97.35, 15.24) * mm});
            skLineSegment(sketch, "E209.9.0.6", {"start": v(101.24, 0) * mm, "end": v(103.84, 0) * mm});
            skLineSegment(sketch, "E209.10.0.0", {"start": v(103.84, 15.24) * mm, "end": v(111.63, 15.24) * mm, "construction": true});
            skLineSegment(sketch, "E209.10.0.1", {"start": v(111.63, 15.24) * mm, "end": v(111.63, 0) * mm});
            skLineSegment(sketch, "E209.10.0.2", {"start": v(107.73, 20.32) * mm, "end": v(111.63, 15.24) * mm});
            skLineSegment(sketch, "E209.10.0.3", {"start": v(103.84, 15.24) * mm, "end": v(107.73, 20.32) * mm});
            skLineSegment(sketch, "E209.10.0.4", {"start": v(103.84, 0) * mm, "end": v(103.84, 15.24) * mm});
            skPoint(sketch, "E209.10.0.5", {"position": v(107.73, 15.24) * mm});
            skLineSegment(sketch, "E209.10.0.6", {"start": v(111.63, 0) * mm, "end": v(114.22, 0) * mm});
            skLineSegment(sketch, "E209.11.0.0", {"start": v(114.22, 15.24) * mm, "end": v(122.01, 15.24) * mm, "construction": true});
            skLineSegment(sketch, "E209.11.0.1", {"start": v(122.01, 15.24) * mm, "end": v(122.01, 0) * mm});
            skLineSegment(sketch, "E209.11.0.2", {"start": v(118.12, 20.32) * mm, "end": v(122.01, 15.24) * mm});
            skLineSegment(sketch, "E209.11.0.3", {"start": v(114.22, 15.24) * mm, "end": v(118.12, 20.32) * mm});
            skLineSegment(sketch, "E209.11.0.4", {"start": v(114.22, 0) * mm, "end": v(114.22, 15.24) * mm});
            skPoint(sketch, "E209.11.0.5", {"position": v(118.12, 15.24) * mm});
            skLineSegment(sketch, "E209.11.0.6", {"start": v(122.01, 0) * mm, "end": v(124.6, 0) * mm});
            skLineSegment(sketch, "E209.12.0.0", {"start": v(124.6, 15.24) * mm, "end": v(132.4, 15.24) * mm, "construction": true});
            skLineSegment(sketch, "E209.12.0.1", {"start": v(132.4, 15.24) * mm, "end": v(132.4, 0) * mm});
            skLineSegment(sketch, "E209.12.0.2", {"start": v(128.5, 20.32) * mm, "end": v(132.4, 15.24) * mm});
            skLineSegment(sketch, "E209.12.0.3", {"start": v(124.6, 15.24) * mm, "end": v(128.5, 20.32) * mm});
            skLineSegment(sketch, "E209.12.0.4", {"start": v(124.6, 0) * mm, "end": v(124.6, 15.24) * mm});
            skPoint(sketch, "E209.12.0.5", {"position": v(128.5, 15.24) * mm});
            skLineSegment(sketch, "E209.12.0.6", {"start": v(132.4, 0) * mm, "end": v(135, 0) * mm});
            skLineSegment(sketch, "E209.13.0.0", {"start": v(135, 15.24) * mm, "end": v(142.78, 15.24) * mm, "construction": true});
            skLineSegment(sketch, "E209.13.0.1", {"start": v(142.78, 15.24) * mm, "end": v(142.78, 0) * mm});
            skLineSegment(sketch, "E209.13.0.2", {"start": v(138.89, 20.32) * mm, "end": v(142.78, 15.24) * mm});
            skLineSegment(sketch, "E209.13.0.3", {"start": v(135, 15.24) * mm, "end": v(138.89, 20.32) * mm});
            skLineSegment(sketch, "E209.13.0.4", {"start": v(135, 0) * mm, "end": v(135, 15.24) * mm});
            skPoint(sketch, "E209.13.0.5", {"position": v(138.89, 15.24) * mm});
            skLineSegment(sketch, "E209.13.0.6", {"start": v(142.78, 0) * mm, "end": v(145.38, 0) * mm});
            skLineSegment(sketch, "E209.14.0.0", {"start": v(145.38, 15.24) * mm, "end": v(153.16, 15.24) * mm, "construction": true});
            skLineSegment(sketch, "E209.14.0.1", {"start": v(153.16, 15.24) * mm, "end": v(153.16, 0) * mm});
            skLineSegment(sketch, "E209.14.0.2", {"start": v(149.27, 20.32) * mm, "end": v(153.16, 15.24) * mm});
            skLineSegment(sketch, "E209.14.0.3", {"start": v(145.38, 15.24) * mm, "end": v(149.27, 20.32) * mm});
            skLineSegment(sketch, "E209.14.0.4", {"start": v(145.38, 0) * mm, "end": v(145.38, 15.24) * mm});
            skPoint(sketch, "E209.14.0.5", {"position": v(149.27, 15.24) * mm});
            skLineSegment(sketch, "E209.14.0.6", {"start": v(153.16, 0) * mm, "end": v(155.76, 0) * mm});
            skLineSegment(sketch, "E209.15.0.0", {"start": v(155.76, 15.24) * mm, "end": v(163.55, 15.24) * mm, "construction": true});
            skLineSegment(sketch, "E209.15.0.1", {"start": v(163.55, 15.24) * mm, "end": v(163.55, 0) * mm});
            skLineSegment(sketch, "E209.15.0.2", {"start": v(159.65, 20.32) * mm, "end": v(163.55, 15.24) * mm});
            skLineSegment(sketch, "E209.15.0.3", {"start": v(155.76, 15.24) * mm, "end": v(159.65, 20.32) * mm});
            skLineSegment(sketch, "E209.15.0.4", {"start": v(155.76, 0) * mm, "end": v(155.76, 15.24) * mm});
            skPoint(sketch, "E209.15.0.5", {"position": v(159.65, 15.24) * mm});
            skLineSegment(sketch, "E209.15.0.6", {"start": v(163.55, 0) * mm, "end": v(166.14, 0) * mm});
            skLineSegment(sketch, "E209.16.0.0", {"start": v(166.14, 15.24) * mm, "end": v(173.93, 15.24) * mm, "construction": true});
            skLineSegment(sketch, "E209.16.0.1", {"start": v(173.93, 15.24) * mm, "end": v(173.93, 0) * mm});
            skLineSegment(sketch, "E209.16.0.2", {"start": v(170.04, 20.32) * mm, "end": v(173.93, 15.24) * mm});
            skLineSegment(sketch, "E209.16.0.3", {"start": v(166.14, 15.24) * mm, "end": v(170.04, 20.32) * mm});
            skLineSegment(sketch, "E209.16.0.4", {"start": v(166.14, 0) * mm, "end": v(166.14, 15.24) * mm});
            skPoint(sketch, "E209.16.0.5", {"position": v(170.04, 15.24) * mm});
            skLineSegment(sketch, "E209.16.0.6", {"start": v(173.93, 0) * mm, "end": v(176.53, 0) * mm});
            skLineSegment(sketch, "E209.17.0.0", {"start": v(176.53, 15.24) * mm, "end": v(184.32, 15.24) * mm, "construction": true});
            skLineSegment(sketch, "E209.17.0.1", {"start": v(184.32, 15.24) * mm, "end": v(184.32, 0) * mm});
            skLineSegment(sketch, "E209.17.0.2", {"start": v(180.42, 20.32) * mm, "end": v(184.32, 15.24) * mm});
            skLineSegment(sketch, "E209.17.0.3", {"start": v(176.53, 15.24) * mm, "end": v(180.42, 20.32) * mm});
            skLineSegment(sketch, "E209.17.0.4", {"start": v(176.53, 0) * mm, "end": v(176.53, 15.24) * mm});
            skPoint(sketch, "E209.17.0.5", {"position": v(180.42, 15.24) * mm});
            skLineSegment(sketch, "E209.17.0.6", {"start": v(184.32, 0) * mm, "end": v(186.91, 0) * mm});
            skLineSegment(sketch, "E209.18.0.0", {"start": v(186.91, 15.24) * mm, "end": v(194.7, 15.24) * mm, "construction": true});
            skLineSegment(sketch, "E209.18.0.1", {"start": v(194.7, 15.24) * mm, "end": v(194.7, 0) * mm});
            skLineSegment(sketch, "E209.18.0.2", {"start": v(190.8, 20.32) * mm, "end": v(194.7, 15.24) * mm});
            skLineSegment(sketch, "E209.18.0.3", {"start": v(186.91, 15.24) * mm, "end": v(190.8, 20.32) * mm});
            skLineSegment(sketch, "E209.18.0.4", {"start": v(186.91, 0) * mm, "end": v(186.91, 15.24) * mm});
            skPoint(sketch, "E209.18.0.5", {"position": v(190.8, 15.24) * mm});
            skLineSegment(sketch, "E209.18.0.6", {"start": v(194.7, 0) * mm, "end": v(197.3, 0) * mm});
            skLineSegment(sketch, "E209.19.0.0", {"start": v(197.3, 15.24) * mm, "end": v(205.08, 15.24) * mm, "construction": true});
            skLineSegment(sketch, "E209.19.0.1", {"start": v(205.08, 15.24) * mm, "end": v(205.08, 0) * mm});
            skLineSegment(sketch, "E209.19.0.2", {"start": v(201.19, 20.32) * mm, "end": v(205.08, 15.24) * mm});
            skLineSegment(sketch, "E209.19.0.3", {"start": v(197.3, 15.24) * mm, "end": v(201.19, 20.32) * mm});
            skLineSegment(sketch, "E209.19.0.4", {"start": v(197.3, 0) * mm, "end": v(197.3, 15.24) * mm});
            skPoint(sketch, "E209.19.0.5", {"position": v(201.19, 15.24) * mm});
            skLineSegment(sketch, "E209.direction1", {"start": v(0, 0) * mm, "end": v(10.38, 0) * mm, "construction": true});
            skLineSegment(sketch, "E210", {"start": v(0, 0) * mm, "end": v(0, -5.08) * mm});
            skLineSegment(sketch, "E211", {"start": v(0, -5.08) * mm, "end": v(30, -5.08) * mm});
            skLineSegment(sketch, "E212", {"start": v(30, -5.08) * mm, "end": v(30, -10.16) * mm});
            skLineSegment(sketch, "E213", {"start": v(30, -10.16) * mm, "end": v(180.16, -10.16) * mm});
            skLineSegment(sketch, "E214", {"start": v(180.16, -10.16) * mm, "end": v(180.16, -5.08) * mm});
            skLineSegment(sketch, "E215", {"start": v(180.16, -5.08) * mm, "end": v(205.08, -5.08) * mm});
            skLineSegment(sketch, "E216", {"start": v(205.08, -5.08) * mm, "end": v(205.08, 0) * mm});
            skSolve(sketch);
        }
        {
            var Q0;
            Q0 = qSketchRegion(id + "F14", true);
            extrude(context, id + "F15", {"entities" : qUnion([Q0]), "depth" : 5.08 * mm});
        }
        {
            var Q0;
            Q0=qCreatedBy(makeId("Front.planeOp"),FACE);
            var sketch = newSketch(context, id + "F16", { "sketchPlane" : qUnion([Q0])});
            skLineSegment(sketch, "E217", {"start": v(0, -110) * mm, "end": v(0, 0) * mm});
            skLineSegment(sketch, "E218", {"start": v(0, 0) * mm, "end": v(180, 0) * mm});
            skLineSegment(sketch, "E219", {"start": v(180, 0) * mm, "end": v(180, -110) * mm});
            skArc(sketch, "E220", {"start": v(0, -110) * mm, "mid": v(9, -119) * mm, "end": v(18, -110) * mm});
            skArc(sketch, "E221.1.0.0", {"start": v(18, -110) * mm, "mid": v(27, -119) * mm, "end": v(36, -110) * mm});
            skArc(sketch, "E221.2.0.0", {"start": v(36, -110) * mm, "mid": v(45, -119) * mm, "end": v(54, -110) * mm});
            skArc(sketch, "E221.3.0.0", {"start": v(54, -110) * mm, "mid": v(63, -119) * mm, "end": v(72, -110) * mm});
            skArc(sketch, "E221.4.0.0", {"start": v(72, -110) * mm, "mid": v(81, -119) * mm, "end": v(90, -110) * mm});
            skArc(sketch, "E221.5.0.0", {"start": v(90, -110) * mm, "mid": v(99, -119) * mm, "end": v(108, -110) * mm});
            skArc(sketch, "E221.6.0.0", {"start": v(108, -110) * mm, "mid": v(117, -119) * mm, "end": v(126, -110) * mm});
            skArc(sketch, "E221.7.0.0", {"start": v(126, -110) * mm, "mid": v(135, -119) * mm, "end": v(144, -110) * mm});
            skArc(sketch, "E221.8.0.0", {"start": v(144, -110) * mm, "mid": v(153, -119) * mm, "end": v(162, -110) * mm});
            skArc(sketch, "E221.9.0.0", {"start": v(162, -110) * mm, "mid": v(171, -119) * mm, "end": v(180, -110) * mm});
            skLineSegment(sketch, "E221.direction1", {"start": v(0, -110) * mm, "end": v(18, -110) * mm, "construction": true});
            skLineSegment(sketch, "E222.bottom", {"start": v(20, -55.28) * mm, "end": v(25.08, -55.28) * mm});
            skLineSegment(sketch, "E222.top", {"start": v(20, -90.28) * mm, "end": v(25.08, -90.28) * mm});
            skLineSegment(sketch, "E222.left", {"start": v(20, -55.28) * mm, "end": v(20, -90.28) * mm});
            skLineSegment(sketch, "E222.right", {"start": v(25.08, -55.28) * mm, "end": v(25.08, -90.28) * mm});
            skLineSegment(sketch, "E223", {"start": v(90, -129.2) * mm, "end": v(90, 14.53) * mm, "construction": true});
            skLineSegment(sketch, "E224.MirrorCS", {"start": v(160, -55.28) * mm, "end": v(154.92, -55.28) * mm});
            skLineSegment(sketch, "E225.MirrorCS", {"start": v(160, -90.28) * mm, "end": v(154.92, -90.28) * mm});
            skLineSegment(sketch, "E226.MirrorCS", {"start": v(160, -55.28) * mm, "end": v(160, -90.28) * mm});
            skLineSegment(sketch, "E227.MirrorCS", {"start": v(154.92, -55.28) * mm, "end": v(154.92, -90.28) * mm});
            skLineSegment(sketch, "E228.MirrorCS", {"start": v(0, 0) * mm, "end": v(0, -110) * mm});
            skSolve(sketch);
        }
        {
            var Q0;
            Q0 = qSketchRegion(id + "F16", true);
            extrude(context, id + "F17", {"entities" : qUnion([Q0]), "depth" : 5.08 * mm});
        }
        {
            var Q0;
            Q0=qCreatedBy(makeId("Top.planeOp"),FACE);
            var sketch = newSketch(context, id + "F18", { "sketchPlane" : qUnion([Q0])});
            skLineSegment(sketch, "E229.bottom", {"start": v(90, 8) * mm, "end": v(-90, 8) * mm});
            skLineSegment(sketch, "E229.top", {"start": v(90, -8) * mm, "end": v(-90, -8) * mm});
            skLineSegment(sketch, "E229.left", {"start": v(90, 8) * mm, "end": v(90, -8) * mm});
            skLineSegment(sketch, "E229.right", {"start": v(-90, 8) * mm, "end": v(-90, -8) * mm});
            skPoint(sketch, "E229.middle", {"position": v(0, 0) * mm});
            skLineSegment(sketch, "E230", {"start": v(0, 14.07) * mm, "end": v(0, -17.25) * mm, "construction": true});
            skLineSegment(sketch, "E231.bottom", {"start": v(70, 2.54) * mm, "end": v(64.92, 2.54) * mm});
            skLineSegment(sketch, "E231.top", {"start": v(70, -2.54) * mm, "end": v(64.92, -2.54) * mm});
            skLineSegment(sketch, "E231.left", {"start": v(70, 2.54) * mm, "end": v(70, -2.54) * mm});
            skLineSegment(sketch, "E231.right", {"start": v(64.92, 2.54) * mm, "end": v(64.92, -2.54) * mm});
            skPoint(sketch, "E231.middle", {"position": v(67.46, 0) * mm});
            skLineSegment(sketch, "E232.MirrorCS", {"start": v(-70, 2.54) * mm, "end": v(-64.92, 2.54) * mm});
            skLineSegment(sketch, "E233.MirrorCS", {"start": v(-70, -2.54) * mm, "end": v(-64.92, -2.54) * mm});
            skLineSegment(sketch, "E234.MirrorCS", {"start": v(-64.92, 2.54) * mm, "end": v(-64.92, -2.54) * mm});
            skLineSegment(sketch, "E235.MirrorCS", {"start": v(-70, 2.54) * mm, "end": v(-70, -2.54) * mm});
            skPoint(sketch, "E236.MirrorP", {"position": v(-67.46, 0) * mm});
            skSolve(sketch);
        }
        {
            var Q0;
            Q0 = qSketchRegion(id + "F18", true);
            extrude(context, id + "F19", {"entities" : qUnion([Q0]), "depth" : 5.08 * mm});
        }
        {
            var Q0;
            Q0=qCreatedBy(makeId("Top.planeOp"),FACE);
            var sketch = newSketch(context, id + "F20", { "sketchPlane" : qUnion([Q0])});
            skLineSegment(sketch, "E237.bottom", {"start": v(0, 0) * mm, "end": v(324, 0) * mm});
            skLineSegment(sketch, "E237.top", {"start": v(0, 277) * mm, "end": v(324, 277) * mm});
            skLineSegment(sketch, "E237.left", {"start": v(0, 0) * mm, "end": v(0, 277) * mm});
            skLineSegment(sketch, "E237.right", {"start": v(324, 0) * mm, "end": v(324, 277) * mm});
            skSolve(sketch);
        }
        {
            var Q0;
            Q0 = qSketchRegion(id + "F20", true);
            extrude(context, id + "F21", {"entities" : qUnion([Q0]), "depth" : 1 * mm});
        }
    });
